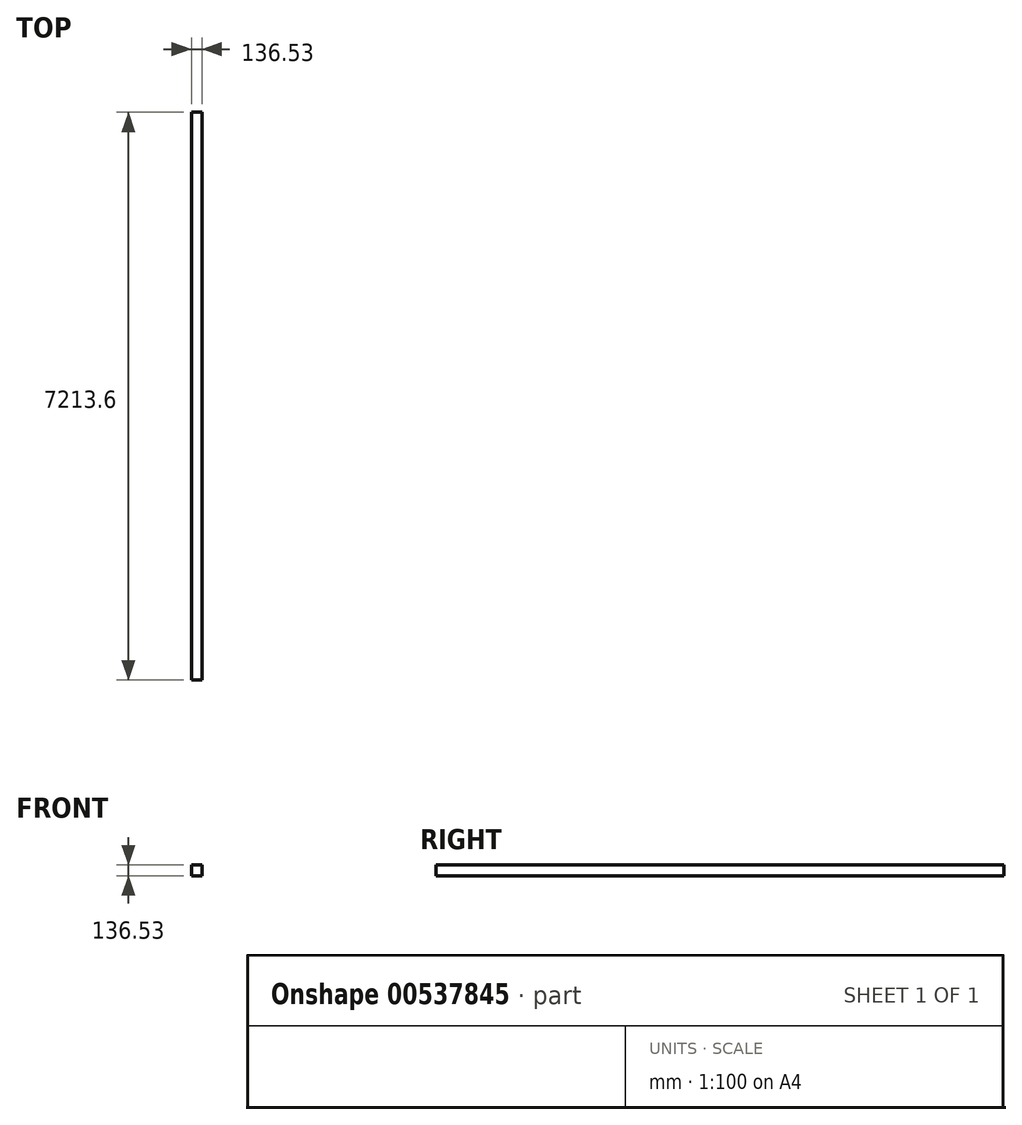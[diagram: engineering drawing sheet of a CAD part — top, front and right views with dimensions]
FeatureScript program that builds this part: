
annotation { "Feature Type Name" : "Feature", "Feature Type Description" : "" }
export const myFeature = defineFeature(function(context is Context, id is Id, definition is map)
    precondition{}
    {
        {
            var Q0;
            Q0=qCreatedBy(makeId("Top.planeOp"),FACE);
            var sketch = newSketch(context, id + "F0", { "sketchPlane" : qUnion([Q0])});
            skLineSegment(sketch, "E0.bottom", {"start": v(-79.34, 5802.2) * mm, "end": v(57.19, 5802.2) * mm});
            skLineSegment(sketch, "E0.top", {"start": v(-79.34, -1411.4) * mm, "end": v(57.19, -1411.4) * mm});
            skLineSegment(sketch, "E0.left", {"start": v(-79.34, 5802.2) * mm, "end": v(-79.34, -1411.4) * mm});
            skLineSegment(sketch, "E0.right", {"start": v(57.19, 5802.2) * mm, "end": v(57.19, -1411.4) * mm});
            skSolve(sketch);
        }
        {
            var Q0;
            Q0 = qSketchRegion(id + "F0", true);
            extrude(context, id + "F1", {"entities" : qUnion([Q0]), "depth" : 136.53 * mm, "offsetDistance" : 25.4 * mm});
        }
    });
